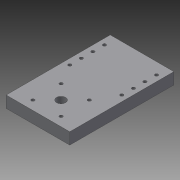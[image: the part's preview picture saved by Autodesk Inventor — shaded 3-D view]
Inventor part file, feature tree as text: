
AUTODESK INVENTOR PART (.ipt)
format: ipt  version: 2015 (Build 190159000, 159)  size: 113,664 bytes
history: native  units: in
note: dims shown in document units (in); Inventor stores cm internally (conversion verified against a paired STEP export)
features: sketch x4, hole x3, extrude x1
ambient origin geometry x8: Origin, YZ Plane, XZ Plane, XY Plane, X Axis, Y Axis, Z Axis, Center Point
bodies: Solid1 (feature_tree)
feature tree (8):
  extrude  "Extrusion1"  Depth=4.5in
  hole  "Hole1"  [1 undecoded]
  hole  "Hole2"  [1 undecoded]
  hole  "Hole3"  [1 undecoded]
  sketch  "Sketch1"  dims[d0=2.75in d1=4.5in]
  sketch  "Sketch2"  dims[d2=0.5in d3=0.0in d7=1.2205in]
  sketch  "Sketch4"  dims[d8=1.22in]
  sketch  "Sketch6"  dims[d9=0.1378in d10=0.75in d11=0.375in d12=0.25in d13=0.5635in d14=1.0in d15=0.8108in d16=0.3937in d17=0.75in d18=0.375in d19=0.25in d20=0.5635in d21=1.0in d22=0.8108in d29=0.5in d30=0.5in d31=0.5in d34=0.25in d35=0.1378in d36=0.75in d37=0.375in d38=0.25in d39=0.5635in d40=1.0in d41=0.8108in d44=0.5in d46=1.0in]
note: 3 required parameter values undecoded (feature->parameter linkage not recoverable at this tier; creation-order binding heuristic only, values carry confidence <= 0.55)
